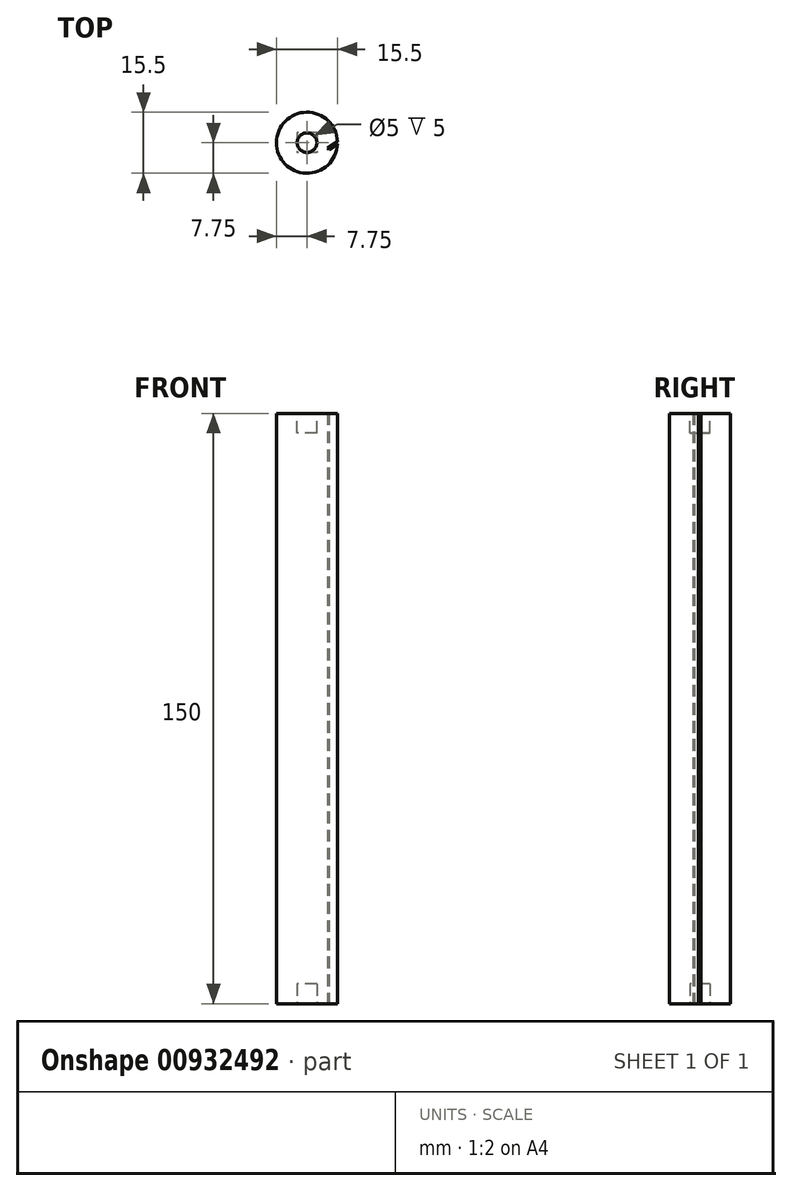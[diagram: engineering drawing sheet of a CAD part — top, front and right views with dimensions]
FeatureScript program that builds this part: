
annotation { "Feature Type Name" : "Feature", "Feature Type Description" : "" }
export const myFeature = defineFeature(function(context is Context, id is Id, definition is map)
    precondition{}
    {
        {
            var Q0;
            Q0=qCreatedBy(makeId("Top.planeOp"),FACE);
            var sketch = newSketch(context, id + "F0", { "sketchPlane" : qUnion([Q0])});
            skArc(sketch, "E0", {"start": v(7.75, 0.25) * mm, "mid": v(-7.75, 0.05) * mm, "end": v(7.74, -0.35) * mm});
            skLineSegment(sketch, "E1", {"start": v(7.75, 0.25) * mm, "end": v(5.27, -1.39) * mm});
            skLineSegment(sketch, "E2.0", {"start": v(7.74, -0.35) * mm, "end": v(5.55, -1.8) * mm});
            skLineSegment(sketch, "E3", {"start": v(5.55, -1.8) * mm, "end": v(5.27, -1.39) * mm});
            skPoint(sketch, "E4.right.start.orphan", {"position": v(-8.75, -0.25) * mm});
            skPoint(sketch, "E5.orphan", {"position": v(-8.75, 0.25) * mm});
            skPoint(sketch, "E4.left.start.orphan", {"position": v(8.75, -0.25) * mm});
            skPoint(sketch, "E4.top.start.orphan", {"position": v(8.75, 0.25) * mm});
            skSolve(sketch);
        }
        {
            var Q0;
            Q0=makeQuery(id+"F0.imprint","IMPRINT",FACE,{"disambiguationData":[TD([[makeQuery(id+"F0.imprint","IMPRINT",EDGE,{"derivedFrom":sQuery(id+"F0.wireOp",EDGE,"E0")}),1.0]])]});
            extrude(context, id + "F1", {"entities" : qUnion([Q0]), "depth" : 150 * mm, "offsetDistance" : 25 * mm});
        }
        {
            var Q0;
            Q0=makeQuery(id+"F1.opExtrude","CAP_FACE",FACE,{"disambiguationData":[OSD([sQuery(id+"F0.wireOp",EDGE,"E0"),sQuery(id+"F0.wireOp",EDGE,"E1"),sQuery(id+"F0.wireOp",EDGE,"E2.0"),sQuery(id+"F0.wireOp",EDGE,"E3")])],"isStart":false});
            var sketch = newSketch(context, id + "F2", { "sketchPlane" : qUnion([Q0])});
            skCircle(sketch, "E6", {"center": v(0, 0) * mm, "radius": 2.5 * mm});
            skSolve(sketch);
        }
        {
            var Q0;
            Q0=makeQuery(id+"F2.imprint","IMPRINT",FACE,{"disambiguationData":[TD([[makeQuery(id+"F2.imprint","IMPRINT",EDGE,{"derivedFrom":sQuery(id+"F2.wireOp",EDGE,"E6")}),1.0]])]});
            extrude(context, id + "F3", {"entities" : qUnion([Q0]), "operationType" : NewBodyOperationType.REMOVE, "oppositeDirection" : true, "depth" : 5 * mm, "offsetDistance" : 25 * mm});
        }
        {
            var Q0;
            Q0=makeQuery(id+"F1.opExtrude","CAP_FACE",FACE,{"disambiguationData":[OSD([sQuery(id+"F0.wireOp",EDGE,"E0"),sQuery(id+"F0.wireOp",EDGE,"E1"),sQuery(id+"F0.wireOp",EDGE,"E2.0"),sQuery(id+"F0.wireOp",EDGE,"E3")])],"isStart":true});
            var sketch = newSketch(context, id + "F4", { "sketchPlane" : qUnion([Q0])});
            skLineSegment(sketch, "E7.bottom", {"start": v(2.5, -2.5) * mm, "end": v(-2.5, -2.5) * mm});
            skLineSegment(sketch, "E7.top", {"start": v(2.5, 2.5) * mm, "end": v(-2.5, 2.5) * mm});
            skLineSegment(sketch, "E7.left", {"start": v(2.5, -2.5) * mm, "end": v(2.5, 2.5) * mm});
            skLineSegment(sketch, "E7.right", {"start": v(-2.5, -2.5) * mm, "end": v(-2.5, 2.5) * mm});
            skPoint(sketch, "E7.middle", {"position": v(0, 0) * mm});
            skSolve(sketch);
        }
        {
            var Q0;
            Q0=makeQuery(id+"F4.imprint","IMPRINT",FACE,{"disambiguationData":[TD([[makeQuery(id+"F4.imprint","IMPRINT",EDGE,{"derivedFrom":sQuery(id+"F4.wireOp",EDGE,"E7.bottom")}),-1.0]])]});
            extrude(context, id + "F5", {"entities" : qUnion([Q0]), "operationType" : NewBodyOperationType.REMOVE, "oppositeDirection" : true, "depth" : 5 * mm, "offsetDistance" : 25 * mm});
        }
    });
